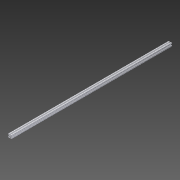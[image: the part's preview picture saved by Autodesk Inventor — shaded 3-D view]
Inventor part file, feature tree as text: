
AUTODESK INVENTOR PART (.ipt)
format: ipt  version: 2013 (Build 170138000, 138)  size: 292,352 bytes
history: native  units: in
note: dims shown in document units (in); Inventor stores cm internally (conversion verified against a paired STEP export)
features: extrude x2, imported_body x1, sketch x1
ambient origin geometry x8: Origin, YZ Plane, XZ Plane, XY Plane, X Axis, Y Axis, Z Axis, Center Point
feature tree (4):
  extrude  "Extrude1"  [1 undecoded]
  extrude  "Extrusion1"  [1 undecoded]
  imported_body  "Base1"
  sketch  "Sketch1"  dims[d0=36.0in d1=0.0in]
note: 2 required parameter values undecoded (feature->parameter linkage not recoverable at this tier; creation-order binding heuristic only, values carry confidence <= 0.55)
